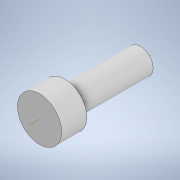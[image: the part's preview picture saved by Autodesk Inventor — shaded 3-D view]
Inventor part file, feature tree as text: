
AUTODESK INVENTOR PART (.ipt)
format: ipt  version: 2021 (Build 250183000, 183)  size: 99,328 bytes
history: native  units: mm
features: revolve x1, sketch x1
ambient origin geometry x8: Origin, YZ Plane, XZ Plane, XY Plane, X Axis, Y Axis, Z Axis, Center Point
bodies: Solid1 (feature_tree)
feature tree (2):
  revolve  "Revolution1"  [1 undecoded]
  sketch  "Sketch1"  dims[d1=3.5mm d2=16.0mm d3=2.0mm d4=4.0mm d5=90.0deg]
note: 1 required parameter value undecoded (feature->parameter linkage not recoverable at this tier; creation-order binding heuristic only, values carry confidence <= 0.55)
